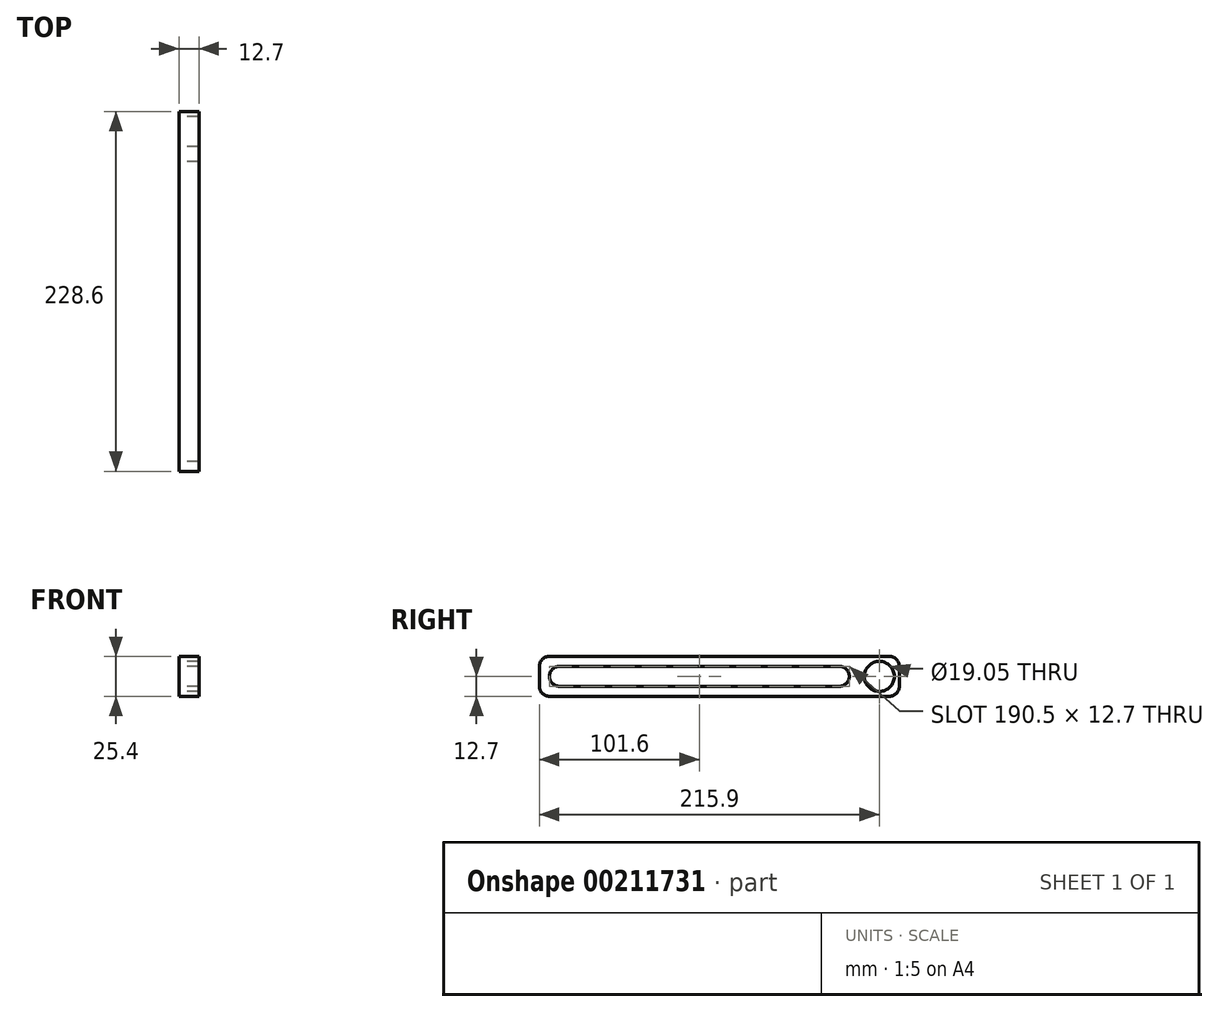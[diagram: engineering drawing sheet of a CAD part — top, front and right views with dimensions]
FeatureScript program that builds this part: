
annotation { "Feature Type Name" : "Feature", "Feature Type Description" : "" }
export const myFeature = defineFeature(function(context is Context, id is Id, definition is map)
    precondition{}
    {
        {
            var Q0;
            Q0=qCreatedBy(makeId("Right.planeOp"),FACE);
            var sketch = newSketch(context, id + "F0", { "sketchPlane" : qUnion([Q0])});
            skLineSegment(sketch, "E0.bottom", {"start": v(107.95, 12.7) * mm, "end": v(-107.95, 12.7) * mm});
            skLineSegment(sketch, "E0.top", {"start": v(107.95, -12.7) * mm, "end": v(-107.95, -12.7) * mm});
            skLineSegment(sketch, "E0.left", {"start": v(114.3, 6.35) * mm, "end": v(114.3, -6.35) * mm});
            skLineSegment(sketch, "E0.right", {"start": v(-114.3, 6.35) * mm, "end": v(-114.3, -6.35) * mm});
            skPoint(sketch, "E0.middle", {"position": v(0, 0) * mm});
            skPoint(sketch, "E1.visualSharp", {"position": v(114.3, 12.7) * mm});
            skArc(sketch, "E1.filletArc", {"start": v(114.3, 6.35) * mm, "mid": v(112.44, 10.84) * mm, "end": v(107.95, 12.7) * mm});
            skPoint(sketch, "E2.visualSharp", {"position": v(114.3, -12.7) * mm});
            skArc(sketch, "E2.filletArc", {"start": v(107.95, -12.7) * mm, "mid": v(112.44, -10.84) * mm, "end": v(114.3, -6.35) * mm});
            skPoint(sketch, "E3.visualSharp", {"position": v(-114.3, 12.7) * mm});
            skArc(sketch, "E3.filletArc", {"start": v(-107.95, 12.7) * mm, "mid": v(-112.44, 10.84) * mm, "end": v(-114.3, 6.35) * mm});
            skPoint(sketch, "E4.visualSharp", {"position": v(-114.3, -12.7) * mm});
            skArc(sketch, "E4.filletArc", {"start": v(-114.3, -6.35) * mm, "mid": v(-112.44, -10.84) * mm, "end": v(-107.95, -12.7) * mm});
            skPoint(sketch, "E5", {"position": v(-114.3, 0) * mm});
            skArc(sketch, "E6", {"start": v(-101.6, 6.35) * mm, "mid": v(-107.95, 0) * mm, "end": v(-101.6, -6.35) * mm});
            skArc(sketch, "E7", {"start": v(76.2, -6.35) * mm, "mid": v(82.55, 0) * mm, "end": v(76.2, 6.35) * mm});
            skCircle(sketch, "E8", {"center": v(101.6, 0) * mm, "radius": 9.53 * mm});
            skLineSegment(sketch, "E9", {"start": v(-101.6, 6.35) * mm, "end": v(76.2, 6.35) * mm});
            skLineSegment(sketch, "E10", {"start": v(-101.6, -6.35) * mm, "end": v(76.2, -6.35) * mm});
            skSolve(sketch);
        }
        {
            var Q0;
            Q0=makeQuery(id+"F0.imprint","IMPRINT",FACE,{"disambiguationData":[TD([[makeQuery(id+"F0.imprint","IMPRINT",EDGE,{"derivedFrom":sQuery(id+"F0.wireOp",EDGE,"E0.bottom")}),1.0]])]});
            extrude(context, id + "F1", {"entities" : qUnion([Q0]), "endBound" : BoundingType.SYMMETRIC, "depth" : 12.7 * mm});
        }
    });
